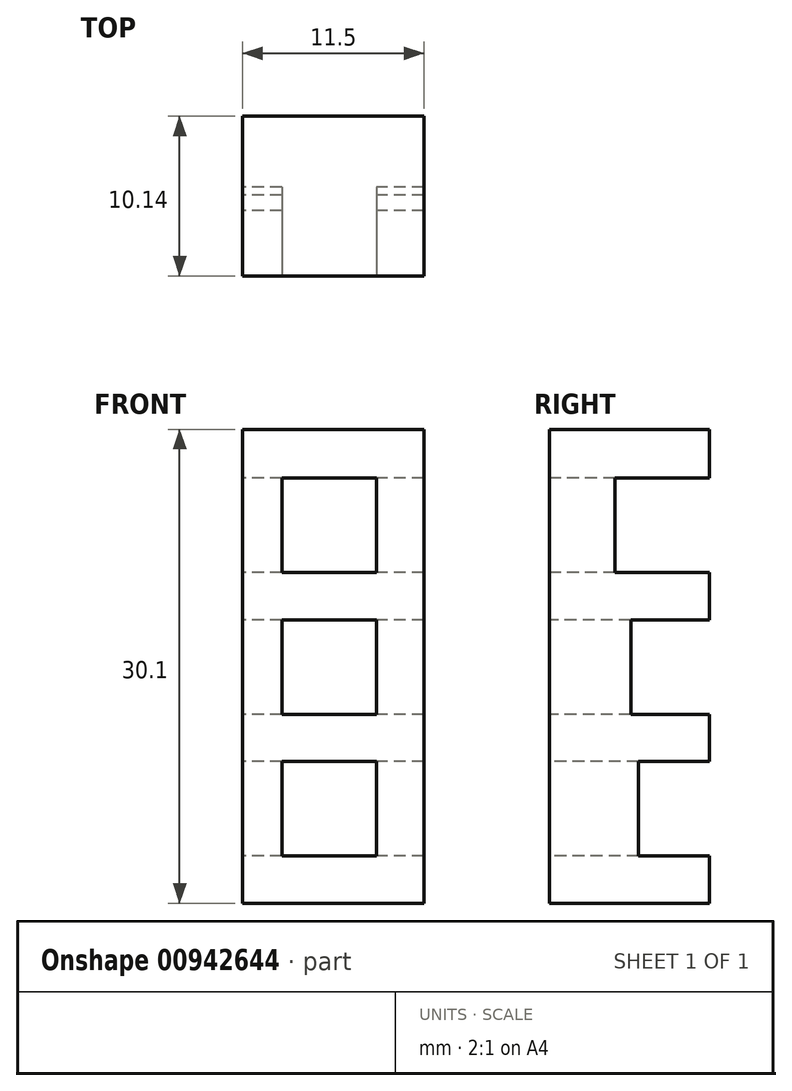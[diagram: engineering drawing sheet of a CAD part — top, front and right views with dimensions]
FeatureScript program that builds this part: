
annotation { "Feature Type Name" : "Feature", "Feature Type Description" : "" }
export const myFeature = defineFeature(function(context is Context, id is Id, definition is map)
    precondition{}
    {
        {
            var Q0;
            Q0=qCreatedBy(makeId("Top.planeOp"),FACE);
            var sketch = newSketch(context, id + "F0", { "sketchPlane" : qUnion([Q0])});
            skLineSegment(sketch, "E0.bottom", {"start": v(10.72, 5.08) * mm, "end": v(-10.72, 5.08) * mm});
            skLineSegment(sketch, "E0.top", {"start": v(10.72, -5.08) * mm, "end": v(-10.72, -5.08) * mm});
            skLineSegment(sketch, "E0.left", {"start": v(10.72, 5.08) * mm, "end": v(10.72, -5.07) * mm});
            skLineSegment(sketch, "E0.right", {"start": v(-10.72, 5.08) * mm, "end": v(-10.72, -5.07) * mm});
            skPoint(sketch, "E0.middle", {"position": v(0, 0) * mm});
            skLineSegment(sketch, "E1.bottom", {"start": v(10.72, -5.08) * mm, "end": v(13.98, -5.08) * mm});
            skLineSegment(sketch, "E1.top", {"start": v(10.72, 7.23) * mm, "end": v(13.98, 7.23) * mm});
            skLineSegment(sketch, "E1.left", {"start": v(10.72, -5.08) * mm, "end": v(10.72, 7.23) * mm});
            skLineSegment(sketch, "E1.right", {"start": v(13.98, -5.08) * mm, "end": v(13.98, 7.23) * mm});
            skLineSegment(sketch, "E2.bottom", {"start": v(13.98, -5.08) * mm, "end": v(17.39, -5.08) * mm});
            skLineSegment(sketch, "E2.top", {"start": v(13.98, 9.24) * mm, "end": v(17.39, 9.24) * mm});
            skLineSegment(sketch, "E2.left", {"start": v(13.98, -5.08) * mm, "end": v(13.98, 9.24) * mm});
            skLineSegment(sketch, "E2.right", {"start": v(17.39, -5.08) * mm, "end": v(17.39, 9.24) * mm});
            skSolve(sketch);
        }
        {
            var Q0;
            Q0 = qSketchRegion(id + "F0", true);
            extrude(context, id + "F1", {"entities" : qUnion([Q0]), "depth" : 30.1 * mm, "offsetDistance" : 25 * mm});
        }
        {
            var Q0;
            Q0=makeQuery(id+"F1.opExtrude","SWEPT_FACE",FACE,{"disambiguationData":[OSD([sQuery(id+"F0.wireOp",EDGE,"E0.right")])]});
            var sketch = newSketch(context, id + "F2", { "sketchPlane" : qUnion([Q0])});
            skLineSegment(sketch, "E3.bottom", {"start": v(-5.08, 3) * mm, "end": v(-0.58, 3) * mm});
            skLineSegment(sketch, "E3.top", {"start": v(-5.08, 9) * mm, "end": v(-0.58, 9) * mm});
            skLineSegment(sketch, "E3.left", {"start": v(-5.08, 3) * mm, "end": v(-5.08, 9) * mm});
            skLineSegment(sketch, "E3.right", {"start": v(-0.58, 3) * mm, "end": v(-0.58, 9) * mm});
            skLineSegment(sketch, "E4.bottom", {"start": v(-5.08, 12) * mm, "end": v(-0.08, 12) * mm});
            skLineSegment(sketch, "E4.top", {"start": v(-5.08, 18) * mm, "end": v(-0.08, 18) * mm});
            skLineSegment(sketch, "E4.left", {"start": v(-5.08, 12) * mm, "end": v(-5.08, 18) * mm});
            skLineSegment(sketch, "E4.right", {"start": v(-0.08, 12) * mm, "end": v(-0.08, 18) * mm});
            skLineSegment(sketch, "E5.bottom", {"start": v(-5.08, 21) * mm, "end": v(0.92, 21) * mm});
            skLineSegment(sketch, "E5.top", {"start": v(-5.08, 27) * mm, "end": v(0.92, 27) * mm});
            skLineSegment(sketch, "E5.left", {"start": v(-5.08, 21) * mm, "end": v(-5.08, 27) * mm});
            skLineSegment(sketch, "E5.right", {"start": v(0.92, 21) * mm, "end": v(0.92, 27) * mm});
            skSolve(sketch);
        }
        {
            var Q0;
            Q0 = qSketchRegion(id + "F2", true);
            extrude(context, id + "F3", {"entities" : qUnion([Q0]), "operationType" : NewBodyOperationType.REMOVE, "oppositeDirection" : true, "depth" : 20 * mm, "offsetDistance" : 25 * mm});
        }
        {
            var Q0;
            Q0=makeQuery(id+"F1.opExtrude","SWEPT_FACE",FACE,{"disambiguationData":[OSD([sQuery(id+"F0.wireOp",EDGE,"E0.top"),sQuery(id+"F0.wireOp",EDGE,"E1.bottom"),sQuery(id+"F0.wireOp",EDGE,"E2.bottom")])]});
            var sketch = newSketch(context, id + "F4", { "sketchPlane" : qUnion([Q0])});
            skLineSegment(sketch, "E6.bottom", {"start": v(-8.22, 3) * mm, "end": v(-2.22, 3) * mm});
            skLineSegment(sketch, "E6.top", {"start": v(-8.22, 9) * mm, "end": v(-2.22, 9) * mm});
            skLineSegment(sketch, "E6.left", {"start": v(-8.22, 3) * mm, "end": v(-8.22, 9) * mm});
            skLineSegment(sketch, "E6.right", {"start": v(-2.22, 3) * mm, "end": v(-2.22, 9) * mm});
            skLineSegment(sketch, "E7.bottom", {"start": v(-8.23, 12) * mm, "end": v(-2.23, 12) * mm});
            skLineSegment(sketch, "E7.top", {"start": v(-8.23, 18) * mm, "end": v(-2.23, 18) * mm});
            skLineSegment(sketch, "E7.left", {"start": v(-8.23, 12) * mm, "end": v(-8.23, 18) * mm});
            skLineSegment(sketch, "E7.right", {"start": v(-2.23, 12) * mm, "end": v(-2.23, 18) * mm});
            skLineSegment(sketch, "E8.bottom", {"start": v(-8.23, 21) * mm, "end": v(-2.23, 21) * mm});
            skLineSegment(sketch, "E8.top", {"start": v(-8.23, 27) * mm, "end": v(-2.23, 27) * mm});
            skLineSegment(sketch, "E8.left", {"start": v(-8.23, 21) * mm, "end": v(-8.23, 27) * mm});
            skLineSegment(sketch, "E8.right", {"start": v(-2.23, 21) * mm, "end": v(-2.23, 27) * mm});
            skSolve(sketch);
        }
        {
            var Q0;
            Q0 = qSketchRegion(id + "F4", true);
            extrude(context, id + "F5", {"entities" : qUnion([Q0]), "operationType" : NewBodyOperationType.REMOVE, "oppositeDirection" : true, "depth" : 25 * mm, "offsetDistance" : 25 * mm});
        }
        {
            var Q0;
            Q0=makeQuery(id+"F1.opExtrude","SWEPT_FACE",FACE,{"disambiguationData":[OSD([sQuery(id+"F0.wireOp",EDGE,"E0.top"),sQuery(id+"F0.wireOp",EDGE,"E1.bottom"),sQuery(id+"F0.wireOp",EDGE,"E2.bottom")])]});
            var sketch = newSketch(context, id + "F6", { "sketchPlane" : qUnion([Q0])});
            skLineSegment(sketch, "E9.bottom", {"start": v(0.77, 37.38) * mm, "end": v(39.07, 37.38) * mm});
            skLineSegment(sketch, "E9.top", {"start": v(0.78, -18.36) * mm, "end": v(39.07, -18.36) * mm});
            skLineSegment(sketch, "E9.left", {"start": v(0.77, 37.38) * mm, "end": v(0.78, -18.36) * mm});
            skLineSegment(sketch, "E9.right", {"start": v(39.07, 37.38) * mm, "end": v(39.07, -18.36) * mm});
            skSolve(sketch);
        }
        {
            var Q0;
            Q0 = qSketchRegion(id + "F6", true);
            extrude(context, id + "F7", {"entities" : qUnion([Q0]), "operationType" : NewBodyOperationType.REMOVE, "oppositeDirection" : true, "depth" : 25 * mm, "offsetDistance" : 25 * mm});
        }
    });
